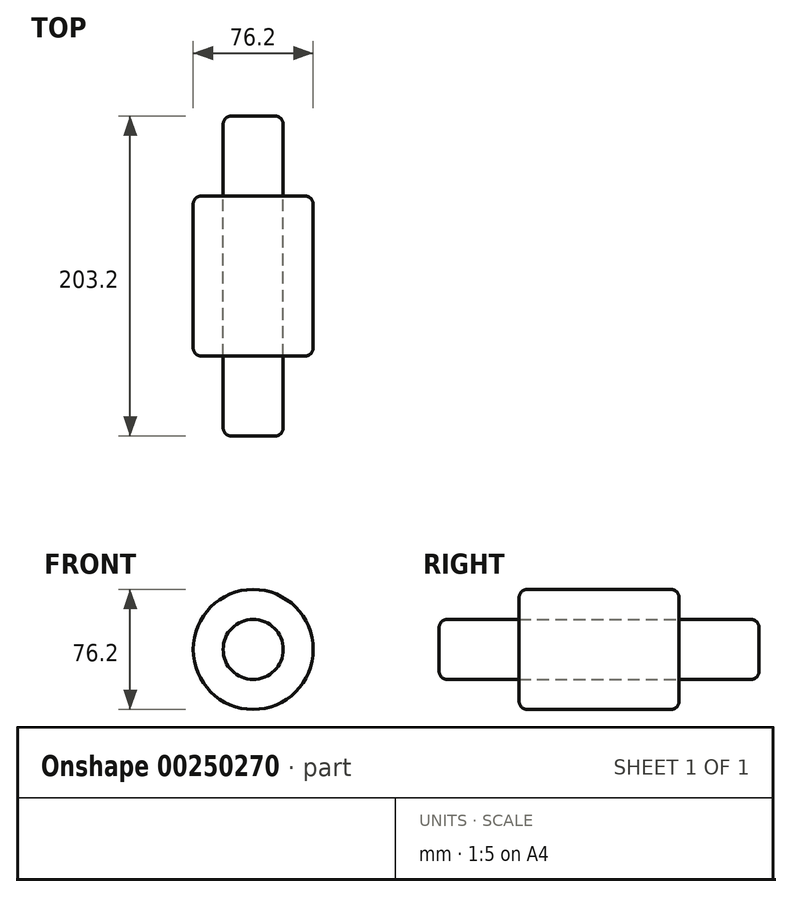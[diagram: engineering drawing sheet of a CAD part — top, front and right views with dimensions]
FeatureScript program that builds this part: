
annotation { "Feature Type Name" : "Feature", "Feature Type Description" : "" }
export const myFeature = defineFeature(function(context is Context, id is Id, definition is map)
    precondition{}
    {
        {
            var Q0;
            Q0=qCreatedBy(makeId("Front.planeOp"),FACE);
            var sketch = newSketch(context, id + "F0", { "sketchPlane" : qUnion([Q0])});
            skCircle(sketch, "E0", {"center": v(0, 0) * mm, "radius": 38.1 * mm});
            skSolve(sketch);
        }
        {
            var Q0;
            Q0=qCreatedBy(makeId("Front.planeOp"),FACE);
            var sketch = newSketch(context, id + "F1", { "sketchPlane" : qUnion([Q0])});
            skCircle(sketch, "E1", {"center": v(0, 0) * mm, "radius": 19.05 * mm});
            skSolve(sketch);
        }
        {
            var Q0;
            Q0 = qSketchRegion(id + "F1", true);
            var Q1;
            Q1 = qSketchRegion(id + "F0", true);
            extrude(context, id + "F2", {"entities" : qUnion([Q0, Q1]), "endBound" : BoundingType.SYMMETRIC, "depth" : 101.6 * mm});
        }
        {
            var Q0;
            Q0=makeQuery(id+"F1.imprint","IMPRINT",FACE,{"disambiguationData":[TD([[makeQuery(id+"F1.imprint","IMPRINT",EDGE,{"derivedFrom":sQuery(id+"F1.wireOp",EDGE,"E1")}),1.0]])]});
            extrude(context, id + "F3", {"entities" : qUnion([Q0]), "endBound" : BoundingType.SYMMETRIC, "depth" : 203.2 * mm});
        }
        {
            var Q0;
            Q0=makeQuery(id+"F2.opExtrude","CAP_EDGE",EDGE,{"disambiguationData":[OSD([sQuery(id+"F0.wireOp",EDGE,"E0")])],"isStart":false});
            var Q1;
            Q1=makeQuery(id+"F2.opExtrude","CAP_FACE",FACE,{"disambiguationData":[OSD([sQuery(id+"F0.wireOp",EDGE,"E0")])],"isStart":true});
            fillet(context, id + "F4", {"entities" : qUnion([Q0, Q1]), "radius" : 5.08 * mm, "tangentPropagation" : true, "allowEdgeOverflow" : false});
        }
        {
            var Q0;
            Q0=makeQuery(id+"F3.opExtrude","CAP_EDGE",EDGE,{"disambiguationData":[OSD([sQuery(id+"F1.wireOp",EDGE,"E1")])],"isStart":true});
            var Q1;
            Q1=makeQuery(id+"F3.opExtrude","CAP_EDGE",EDGE,{"disambiguationData":[OSD([sQuery(id+"F1.wireOp",EDGE,"E1")])],"isStart":false});
            fillet(context, id + "F5", {"entities" : qUnion([Q0, Q1]), "radius" : 5.08 * mm, "tangentPropagation" : true, "allowEdgeOverflow" : false});
        }
    });
